# Revit family: Haworth_Cappellini_Ribbon_Stool_High_AP_PRELIMINARY
name_source: partatom
category: Furniture
revit_build: Autodesk Revit 2018 (Build: 20170223_1515(x64)
units: mm (PartAtom-declared; Revit-internal decimal feet)

## family parameters
Always vertical = Yes
Cut with Voids When Loaded = No
OmniClass Number = 23.40.70.14.64.11
OmniClass Title = Office Furniture
Room Calculation Point = No
Shared = No
Work Plane-Based = No

## types (2) — shared parameters
Actual Depth = 375 mm  [stored 1.23031 ft]
Actual Height = 770 mm  [stored 2.52625 ft]
Actual Width = 375 mm  [stored 1.23031 ft]
Assembly Code = E2020200
Bar Bottom = 284 mm
Bar Height = 319 mm
Description = Haworth - Cappellini - Ribbon - Stool High
Manufacturer = Haworth
Model = RI_1LL
Revision Number = 1
Seat Thickness = 35 mm  [stored 0.114829 ft]
Size = Verify Final Dim. w/ Haworth
URL = https://www.haworth.com
URL - Product = https://www.haworth.com
Warranty = http://www.haworth.com

## per-type parameters (varying)
| type | Cushion |
| Stool High - With Cushion | Yes |
| Stool High - No Cushion | No |

note: [stored X ft] marks values corroborated as IEEE doubles in the binary element streams (Revit-internal decimal feet)

## geometry (parser evidence)
native form markers: Sweep x3
no freeform markers — native parametric forms only
